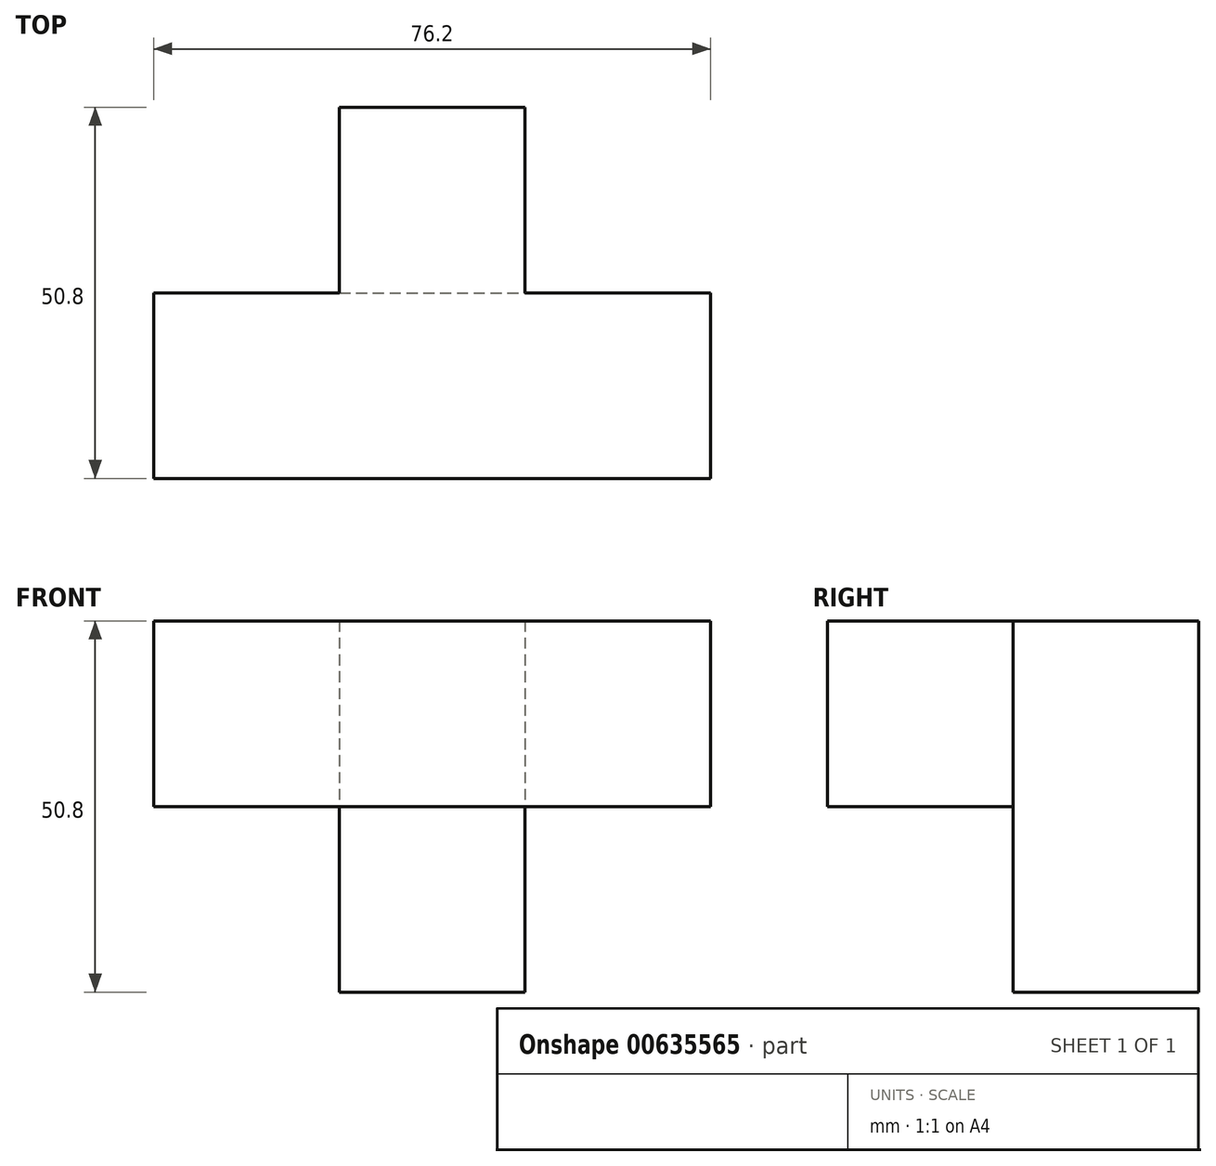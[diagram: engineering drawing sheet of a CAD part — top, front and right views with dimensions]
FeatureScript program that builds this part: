
annotation { "Feature Type Name" : "Feature", "Feature Type Description" : "" }
export const myFeature = defineFeature(function(context is Context, id is Id, definition is map)
    precondition{}
    {
        {
            var Q0;
            Q0=qCreatedBy(makeId("Top.planeOp"),FACE);
            var sketch = newSketch(context, id + "F0", { "sketchPlane" : qUnion([Q0])});
            skLineSegment(sketch, "E0.bottom", {"start": v(0, 0) * mm, "end": v(76.2, 0) * mm});
            skLineSegment(sketch, "E0.top", {"start": v(0, 25.4) * mm, "end": v(76.2, 25.4) * mm});
            skLineSegment(sketch, "E0.left", {"start": v(0, 0) * mm, "end": v(0, 25.4) * mm});
            skLineSegment(sketch, "E0.right", {"start": v(76.2, 0) * mm, "end": v(76.2, 25.4) * mm});
            skLineSegment(sketch, "E1.bottom", {"start": v(25.4, 0) * mm, "end": v(50.8, 0) * mm});
            skLineSegment(sketch, "E1.top", {"start": v(25.4, 50.8) * mm, "end": v(50.8, 50.8) * mm});
            skLineSegment(sketch, "E1.left", {"start": v(25.4, 0) * mm, "end": v(25.4, 50.8) * mm});
            skLineSegment(sketch, "E1.right", {"start": v(50.8, 0) * mm, "end": v(50.8, 50.8) * mm});
            skSolve(sketch);
        }
        {
            var Q0;
            Q0 = qSketchRegion(id + "F0", true);
            extrude(context, id + "F1", {"entities" : qUnion([Q0]), "depth" : 25.4 * mm, "offsetDistance" : 25.4 * mm});
        }
        {
            var Q0;
            {var subQ5=sQuery(id+"F0.wireOp",EDGE,"E1.top");Q0=makeQuery(id+"F0.imprint","IMPRINT",FACE,{"disambiguationData":[TD([[makeQuery(id+"F0.imprint","IMPRINT",EDGE,{"derivedFrom":subQ5}),-1.0]])]});}
            extrude(context, id + "F2", {"entities" : qUnion([Q0]), "operationType" : NewBodyOperationType.ADD, "oppositeDirection" : true, "depth" : 25.4 * mm, "offsetDistance" : 25.4 * mm});
        }
    });
